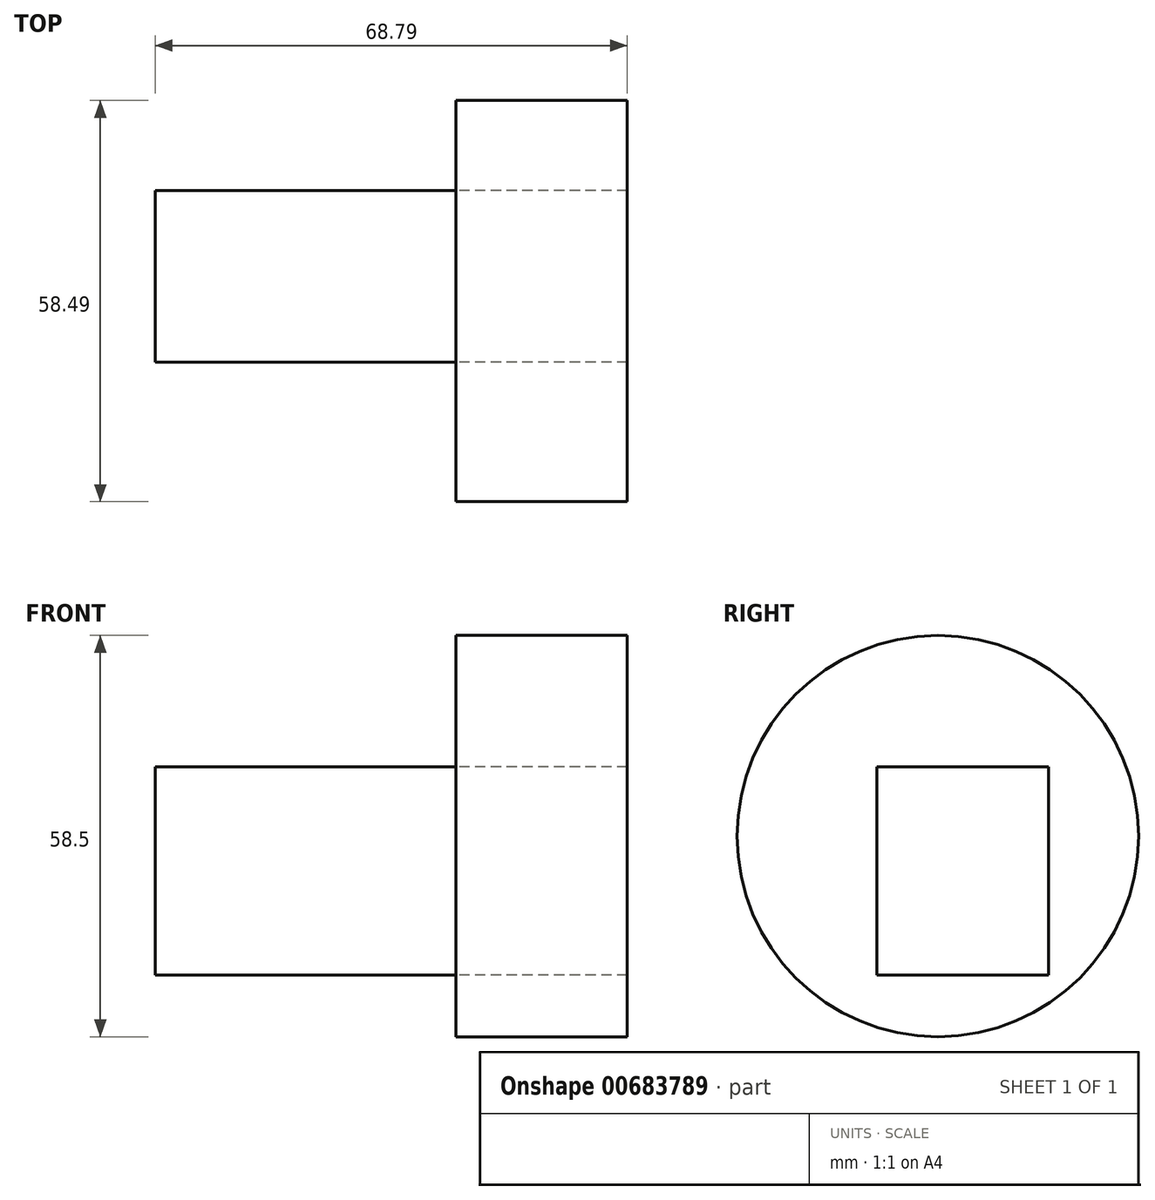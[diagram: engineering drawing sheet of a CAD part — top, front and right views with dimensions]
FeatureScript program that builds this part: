
annotation { "Feature Type Name" : "Feature", "Feature Type Description" : "" }
export const myFeature = defineFeature(function(context is Context, id is Id, definition is map)
    precondition{}
    {
        {
            var Q0;
            Q0=qCreatedBy(makeId("Front.planeOp"),FACE);
            var sketch = newSketch(context, id + "F0", { "sketchPlane" : qUnion([Q0])});
            skLineSegment(sketch, "E0.bottom", {"start": v(0, -2.75) * mm, "end": v(43.8, -2.75) * mm});
            skLineSegment(sketch, "E0.top", {"start": v(0, 27.6) * mm, "end": v(43.8, 27.6) * mm});
            skLineSegment(sketch, "E0.left", {"start": v(0, -2.75) * mm, "end": v(0, 27.6) * mm});
            skLineSegment(sketch, "E0.right", {"start": v(43.8, -2.75) * mm, "end": v(43.8, 27.6) * mm});
            skSolve(sketch);
        }
        {
            var Q0;
            Q0=makeQuery(id+"F0.imprint","IMPRINT",FACE,{"disambiguationData":[TD([[makeQuery(id+"F0.imprint","IMPRINT",EDGE,{"derivedFrom":sQuery(id+"F0.wireOp",EDGE,"E0.bottom")}),1.0]])]});
            extrude(context, id + "F1", {"entities" : qUnion([Q0]), "depth" : 25 * mm, "offsetDistance" : 25 * mm});
        }
        {
            var Q0;
            Q0=makeQuery(id+"F1.opExtrude","SWEPT_FACE",FACE,{"disambiguationData":[OSD([sQuery(id+"F0.wireOp",EDGE,"E0.right")])]});
            var sketch = newSketch(context, id + "F2", { "sketchPlane" : qUnion([Q0])});
            skCircle(sketch, "E1", {"center": v(-16.11, 17.49) * mm, "radius": 29.25 * mm});
            skSolve(sketch);
        }
        {
            var Q0;
            Q0=makeQuery(id+"F2.imprint","IMPRINT",FACE,{"disambiguationData":[TD([[makeQuery(id+"F2.imprint","IMPRINT",EDGE,{"derivedFrom":sQuery(id+"F2.wireOp",EDGE,"E1")}),1.0]])]});
            extrude(context, id + "F3", {"entities" : qUnion([Q0]), "depth" : 25 * mm, "offsetDistance" : 25 * mm});
        }
    });
